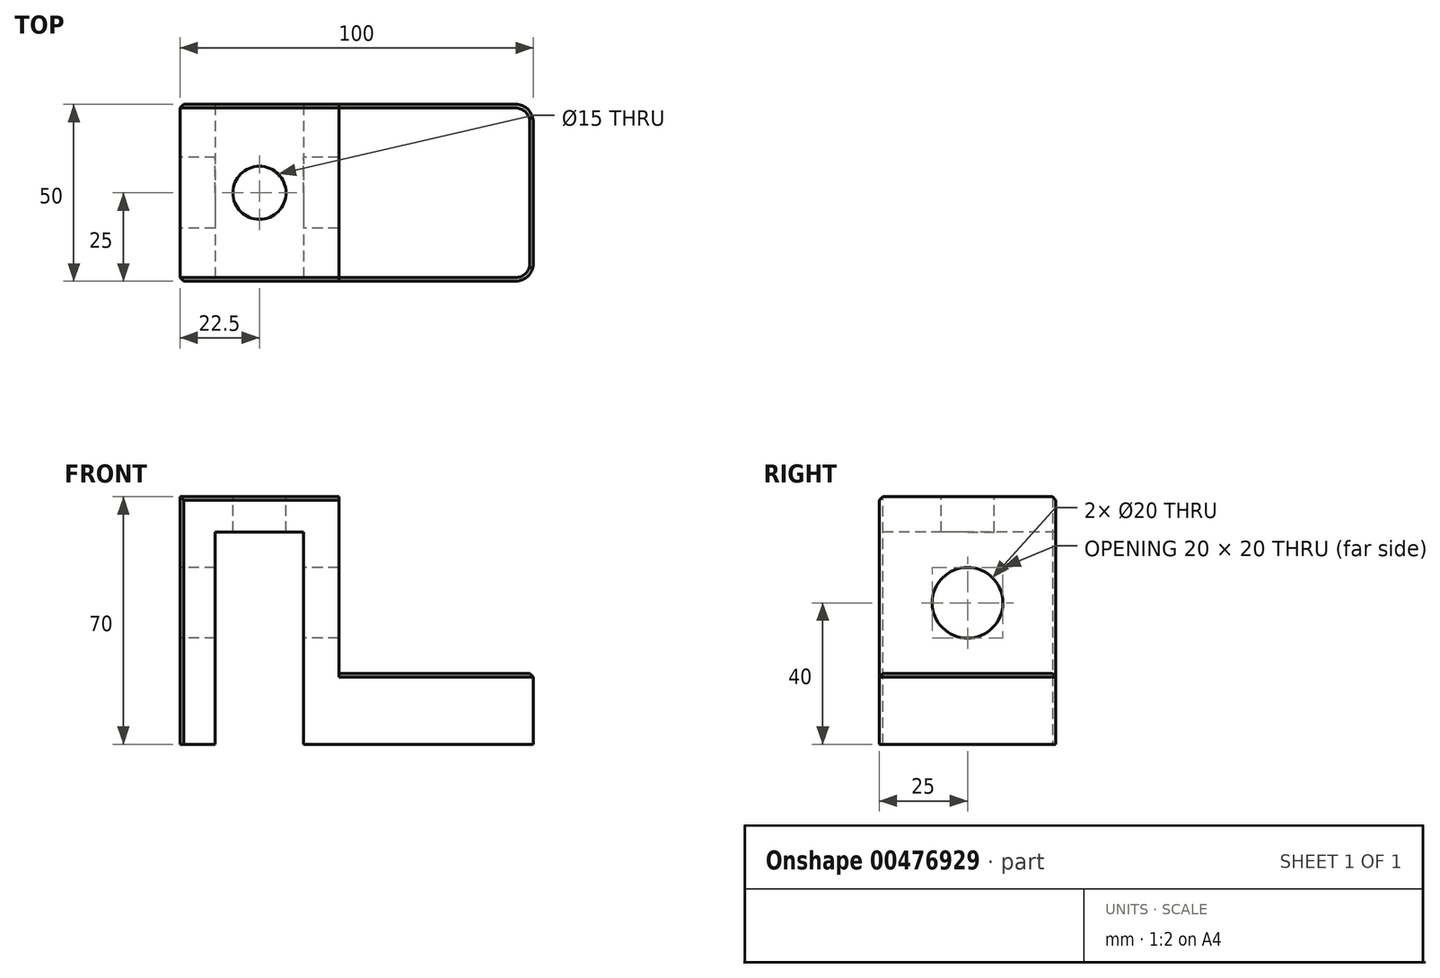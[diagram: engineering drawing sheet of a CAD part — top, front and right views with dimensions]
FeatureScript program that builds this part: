
annotation { "Feature Type Name" : "Feature", "Feature Type Description" : "" }
export const myFeature = defineFeature(function(context is Context, id is Id, definition is map)
    precondition{}
    {
        {
            var Q0;
            Q0=qCreatedBy(makeId("Top.planeOp"),FACE);
            var sketch = newSketch(context, id + "F0", { "sketchPlane" : qUnion([Q0])});
            skLineSegment(sketch, "E0.bottom", {"start": v(0, 0) * mm, "end": v(100, 0) * mm});
            skLineSegment(sketch, "E0.top", {"start": v(0, 50) * mm, "end": v(100, 50) * mm});
            skLineSegment(sketch, "E0.left", {"start": v(0, 0) * mm, "end": v(0, 50) * mm});
            skLineSegment(sketch, "E0.right", {"start": v(100, 0) * mm, "end": v(100, 50) * mm});
            skSolve(sketch);
        }
        {
            var Q0;
            Q0=makeQuery(id+"F0.imprint","IMPRINT",FACE,{"disambiguationData":[TD([[makeQuery(id+"F0.imprint","IMPRINT",EDGE,{"derivedFrom":sQuery(id+"F0.wireOp",EDGE,"E0.bottom")}),1.0]])]});
            extrude(context, id + "F1", {"entities" : qUnion([Q0]), "depth" : 20 * mm});
        }
        {
            var Q0;
            Q0=makeQuery(id+"F1.opExtrude","CAP_FACE",FACE,{"disambiguationData":[OSD([sQuery(id+"F0.wireOp",EDGE,"E0.bottom"),sQuery(id+"F0.wireOp",EDGE,"E0.top"),sQuery(id+"F0.wireOp",EDGE,"E0.left"),sQuery(id+"F0.wireOp",EDGE,"E0.right")])],"isStart":false});
            var sketch = newSketch(context, id + "F2", { "sketchPlane" : qUnion([Q0])});
            skLineSegment(sketch, "E1.bottom", {"start": v(0, 0) * mm, "end": v(45, 0) * mm});
            skLineSegment(sketch, "E1.top", {"start": v(0, 50) * mm, "end": v(45, 50) * mm});
            skLineSegment(sketch, "E1.left", {"start": v(0, 0) * mm, "end": v(0, 50) * mm});
            skLineSegment(sketch, "E1.right", {"start": v(45, 0) * mm, "end": v(45, 50) * mm});
            skSolve(sketch);
        }
        {
            var Q0;
            Q0 = qSketchRegion(id + "F2", true);
            extrude(context, id + "F3", {"entities" : qUnion([Q0]), "operationType" : NewBodyOperationType.ADD, "depth" : 50 * mm});
        }
        {
            var Q0;
            Q0=makeQuery(id+"F3.boolean.opBoolean","MERGE",FACE,{"derivedFrom":[makeQuery(id+"F1.opExtrude","SWEPT_FACE",FACE,{"disambiguationData":[OSD([sQuery(id+"F0.wireOp",EDGE,"E0.bottom")])]}),makeQuery(id+"F3.opExtrude","SWEPT_FACE",FACE,{"disambiguationData":[OSD([sQuery(id+"F2.wireOp",EDGE,"E1.bottom")])]})]});
            var sketch = newSketch(context, id + "F4", { "sketchPlane" : qUnion([Q0])});
            skLineSegment(sketch, "E2.bottom", {"start": v(10, 0) * mm, "end": v(35, 0) * mm});
            skLineSegment(sketch, "E2.top", {"start": v(10, 60) * mm, "end": v(35, 60) * mm});
            skLineSegment(sketch, "E2.left", {"start": v(10, 0) * mm, "end": v(10, 60) * mm});
            skLineSegment(sketch, "E2.right", {"start": v(35, 0) * mm, "end": v(35, 60) * mm});
            skSolve(sketch);
        }
        {
            var Q0;
            Q0=makeQuery(id+"F4.imprint","IMPRINT",FACE,{"disambiguationData":[TD([[makeQuery(id+"F4.imprint","IMPRINT",EDGE,{"derivedFrom":sQuery(id+"F4.wireOp",EDGE,"E2.bottom")}),1.0]])]});
            extrude(context, id + "F5", {"entities" : qUnion([Q0]), "operationType" : NewBodyOperationType.REMOVE, "endBound" : BoundingType.THROUGH_ALL, "oppositeDirection" : true, "depth" : 25 * mm});
        }
        {
            var Q0;
            Q0=makeQuery(id+"F3.boolean.opBoolean","MERGE",FACE,{"derivedFrom":[makeQuery(id+"F1.opExtrude","SWEPT_FACE",FACE,{"disambiguationData":[OSD([sQuery(id+"F0.wireOp",EDGE,"E0.left")])]}),makeQuery(id+"F3.opExtrude","SWEPT_FACE",FACE,{"disambiguationData":[OSD([sQuery(id+"F2.wireOp",EDGE,"E1.left")])]})]});
            var sketch = newSketch(context, id + "F6", { "sketchPlane" : qUnion([Q0])});
            skCircle(sketch, "E3", {"center": v(-25, 40) * mm, "radius": 10 * mm});
            skSolve(sketch);
        }
        {
            var Q0;
            Q0 = qSketchRegion(id + "F6", true);
            var Q1;
            Q1=makeQuery(id+"F5.boolean.opBoolean","COPY",FACE,{"derivedFrom":makeQuery(id+"F5.opExtrude","SWEPT_FACE",FACE,{"disambiguationData":[OSD([sQuery(id+"F4.wireOp",EDGE,"E2.right")])]})});
            extrude(context, id + "F7", {"entities" : qUnion([Q0]), "operationType" : NewBodyOperationType.REMOVE, "endBound" : BoundingType.THROUGH_ALL, "oppositeDirection" : true, "endBoundEntityFace" : qUnion([Q1]), "depth" : 25 * mm});
        }
        {
            var Q0;
            Q0=makeQuery(id+"F3.opExtrude","CAP_FACE",FACE,{"disambiguationData":[OSD([sQuery(id+"F2.wireOp",EDGE,"E1.bottom"),sQuery(id+"F2.wireOp",EDGE,"E1.top"),sQuery(id+"F2.wireOp",EDGE,"E1.left"),sQuery(id+"F2.wireOp",EDGE,"E1.right")])],"isStart":false});
            var sketch = newSketch(context, id + "F8", { "sketchPlane" : qUnion([Q0])});
            skLineSegment(sketch, "E4", {"start": v(45, 50) * mm, "end": v(0, 0) * mm, "construction": true});
            skLineSegment(sketch, "E5", {"start": v(45, 0) * mm, "end": v(0, 50) * mm, "construction": true});
            skCircle(sketch, "E6", {"center": v(22.5, 25) * mm, "radius": 7.5 * mm});
            skSolve(sketch);
        }
        {
            var Q0;
            Q0 = qSketchRegion(id + "F8", true);
            var Q1;
            Q1=makeQuery(id+"F5.boolean.opBoolean","COPY",FACE,{"derivedFrom":makeQuery(id+"F5.opExtrude","SWEPT_FACE",FACE,{"disambiguationData":[OSD([sQuery(id+"F4.wireOp",EDGE,"E2.top")])]})});
            extrude(context, id + "F9", {"entities" : qUnion([Q0]), "operationType" : NewBodyOperationType.REMOVE, "endBound" : BoundingType.UP_TO_SURFACE, "oppositeDirection" : true, "endBoundEntityFace" : qUnion([Q1]), "depth" : 25 * mm});
        }
        {
            var Q0;
            Q0=makeQuery(id+"F1.opExtrude","SWEPT_EDGE",EDGE,{"disambiguationData":[OSD([sQuery(id+"F0.wireOp",EDGE,"E0.bottom"),sQuery(id+"F0.wireOp",EDGE,"E0.right")])]});
            var Q1;
            Q1=makeQuery(id+"F1.opExtrude","SWEPT_EDGE",EDGE,{"disambiguationData":[OSD([sQuery(id+"F0.wireOp",EDGE,"E0.top"),sQuery(id+"F0.wireOp",EDGE,"E0.right")])]});
            fillet(context, id + "F10", {"entities" : qUnion([Q0, Q1]), "radius" : 5 * mm, "tangentPropagation" : true, "allowEdgeOverflow" : false});
        }
        {
            var Q0;
            Q0=makeQuery(id+"F3.boolean.opBoolean","MERGE",EDGE,{"derivedFrom":[makeQuery(id+"F1.opExtrude","SWEPT_EDGE",EDGE,{"disambiguationData":[OSD([sQuery(id+"F0.wireOp",EDGE,"E0.bottom"),sQuery(id+"F0.wireOp",EDGE,"E0.left")])]}),makeQuery(id+"F3.opExtrude","SWEPT_EDGE",EDGE,{"disambiguationData":[OSD([sQuery(id+"F2.wireOp",EDGE,"E1.bottom"),sQuery(id+"F2.wireOp",EDGE,"E1.left")])]})]});
            var Q1;
            Q1=makeQuery(id+"F3.opExtrude","CAP_EDGE",EDGE,{"disambiguationData":[OSD([sQuery(id+"F2.wireOp",EDGE,"E1.bottom")])],"isStart":false});
            var Q2;
            Q2=makeQuery(id+"F3.boolean.opBoolean","MERGE",EDGE,{"derivedFrom":[makeQuery(id+"F1.opExtrude","SWEPT_EDGE",EDGE,{"disambiguationData":[OSD([sQuery(id+"F0.wireOp",EDGE,"E0.top"),sQuery(id+"F0.wireOp",EDGE,"E0.left")])]}),makeQuery(id+"F3.opExtrude","SWEPT_EDGE",EDGE,{"disambiguationData":[OSD([sQuery(id+"F2.wireOp",EDGE,"E1.top"),sQuery(id+"F2.wireOp",EDGE,"E1.left")])]})]});
            var Q3;
            Q3=makeQuery(id+"F3.opExtrude","CAP_EDGE",EDGE,{"disambiguationData":[OSD([sQuery(id+"F2.wireOp",EDGE,"E1.top")])],"isStart":false});
            var Q4;
            Q4=makeQuery(id+"F1.opExtrude","CAP_EDGE",EDGE,{"disambiguationData":[OSD([sQuery(id+"F0.wireOp",EDGE,"E0.top")])],"isStart":false});
            var Q5;
            Q5=makeQuery(id+"F1.opExtrude","CAP_EDGE",EDGE,{"disambiguationData":[OSD([sQuery(id+"F0.wireOp",EDGE,"E0.bottom")])],"isStart":false});
            chamfer(context, id + "F11", {"entities" : qUnion([Q0, Q1, Q2, Q3, Q4, Q5]), "width" : 1 * mm, "tangentPropagation" : true});
        }
    });
